# Revit family: Electrical_Equipment-Poke_Through-Hubbell_Wiring-System_One-S1PTAV
name_source: partatom
category: Electrical Fixtures
revit_build: Autodesk Revit 2015 (Build: 20140606_1530(x64)
units: mm (PartAtom-declared; Revit-internal decimal feet)

## types (1)
- FIT AV
    Apparent Load = 4800 VA
    Assembly Code = D5020115
    Conduit Connector 1 Description = Conduit Connector 1
    Conduit Connector 2 Description = Conduit Connector 2
    Conduit Connector 3 Description = Conduit Connector 3
    Cover Material = Metal-Hubbell-Aluminum
    Default Elevation = 0' - 0"
    Description = System One - 4" Poke Through
    Electrical Connector Description = Power Connector
    Hardware Material = Metal-Hubbell-Steel
    Junction Box Horizontal = 0' - 1"
    Junction Box Vertical = 0' - 10 15/32"
    Load Classification = Power
    Manufacturer = Hubbell-Wiring
    Model = S1PTAV
    Number of Poles = 1
    Poke Through = Poke Through FIT AV : 6Plug
    Power Factor = 1
    Product Documentation Link = http://ecatalog.hubbell-wiring.com
    Product Page URL = http://ecatalog.hubbell-wiring.com
    Product data url = https://bimobject.com
    Subplate = Subplate : S1SP
    URL = http://www.hubbell-wiring.com
    Voltage = 120 V

## geometry (parser evidence)
native form markers: Blend x30, Sweep x22
no freeform markers — native parametric forms only
